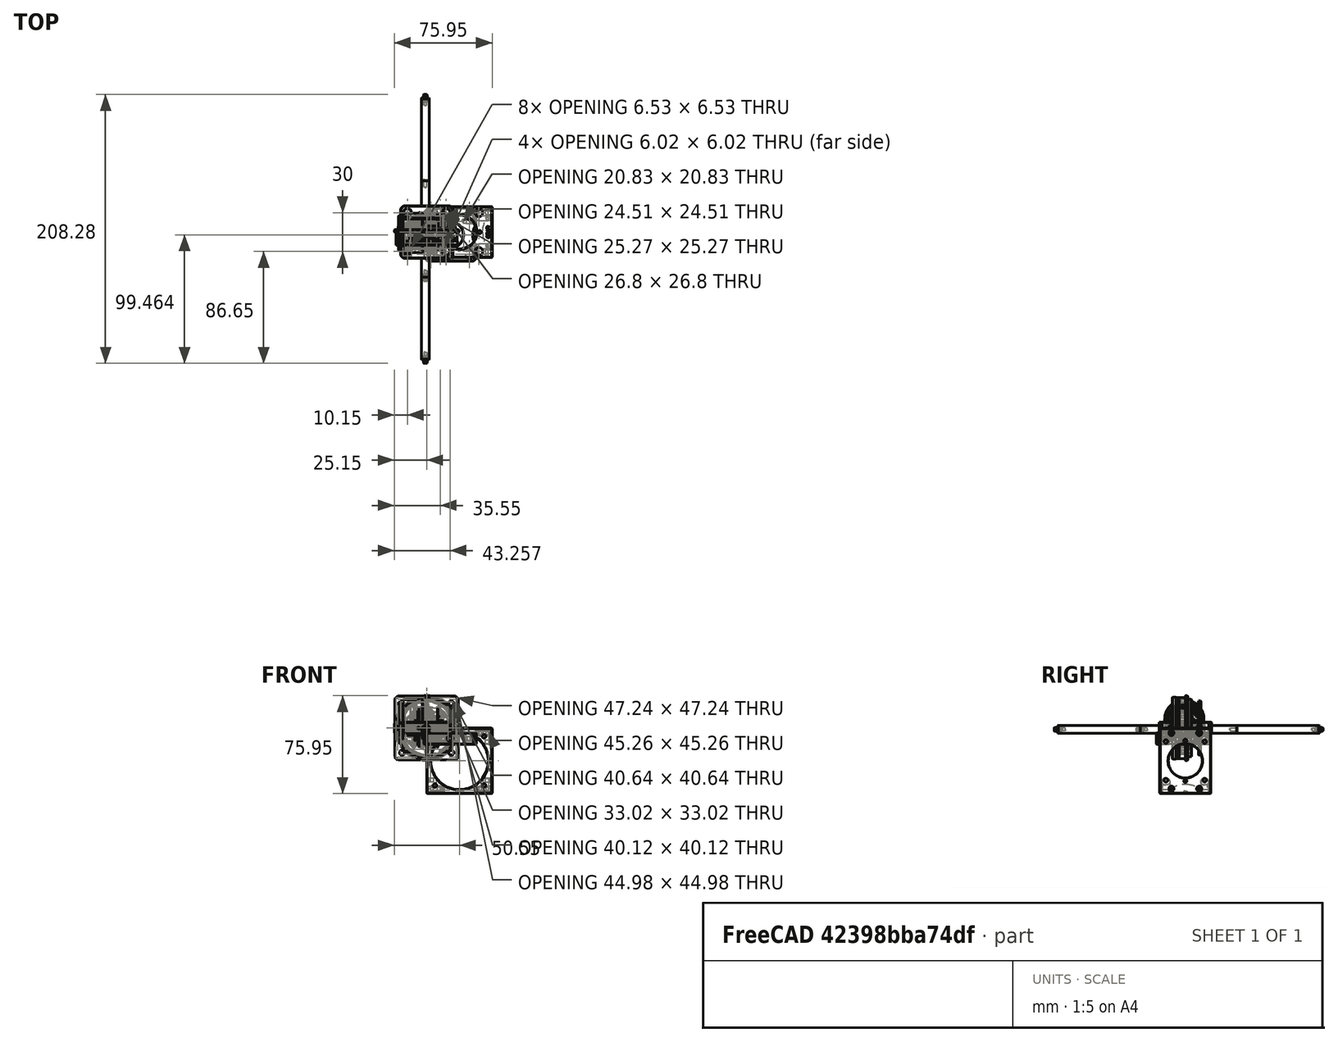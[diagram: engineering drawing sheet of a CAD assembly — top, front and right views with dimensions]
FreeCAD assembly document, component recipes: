
FREECAD ASSEMBLY — COMPONENT RECIPES ("optical-system")

This assembly document has 22 components, labeled P0..P21 below (a component is one placed body or linked part). 1 of them carries a construction recipe — the FreeCAD feature program that regenerates the part from scratch, quoted from this document or its linked companion documents; the rest are supplied as boundary geometry only. No exploded tour is included for this assembly.
COMPONENT P0 — geometry summary ("AC254-040-A-ML001"; no construction recipe available for this part):
  bounding box: 30.5 x 30.5 x 18.5 mm
  tessellated surface: 17,778 triangles
  volume: 9000 mm^3 (52% of its bounding box)
  symmetry: revolution-symmetric about the z axis through its bounding-box center; mirror-symmetric across its x mid-plane, y mid-plane
COMPONENT P1 — geometry summary ("AC254-040-A-ML002"; no construction recipe available for this part):
  bounding box: 30.5 x 30.5 x 18.5 mm
  tessellated surface: 17,778 triangles
  volume: 9000 mm^3 (52% of its bounding box)
  symmetry: revolution-symmetric about the z axis through its bounding-box center; mirror-symmetric across its x mid-plane, y mid-plane
COMPONENT P2 — geometry summary ("AC254-060-A-ML-001"; no construction recipe available for this part):
  bounding box: 30.5 x 30.5 x 17.8 mm
  tessellated surface: 17,160 triangles
  volume: 8517 mm^3 (51% of its bounding box)
  symmetry: revolution-symmetric about the y axis through its bounding-box center; mirror-symmetric across its x mid-plane, z mid-plane
COMPONENT P3 — geometry summary ("B3CR-001"; no construction recipe available for this part):
  bounding box: 50.3 x 50.3 x 14.7 mm
  tessellated surface: 65,470 triangles
  volume: 24011 mm^3 (64% of its bounding box)
COMPONENT P4 — recipe-attached ("BST10R002", modeled in this document).
Construction recipe (the document's own serialized feature program — sketch geometry with constraints, then the solid features built on it; lengths are millimeters unless a unit is written):

FEATURE [PartDesign::FeatureBase] BaseFeature
  BaseFeature = -> Part__Feature051
  Suppressed = false
FEATURE [Sketcher::SketchObject] Sketch
  ArcFitTolerance = 1e-06
  AttachmentSupport = -> [BaseFeature]
  FullyConstrained = true
  MakeInternals = false
  MapMode = 5
  Placement = pos=(0,-12.5,0) rot=(1,0,0;1.5708rad)
  sketch-geometry (5):
    g0: LineSegment StartX=-18 StartY=-0.75 StartZ=0 EndX=18 EndY=-0.75 EndZ=0
    g1: LineSegment StartX=18 StartY=-0.75 StartZ=0 EndX=18 EndY=0.75 EndZ=0
    g2: LineSegment StartX=18 StartY=0.75 StartZ=0 EndX=-18 EndY=0.75 EndZ=0
    g3: LineSegment StartX=-18 StartY=0.75 StartZ=0 EndX=-18 EndY=-0.75 EndZ=0
    g4: GeomPoint [constr] X=0 Y=0 Z=0
  constraints (12):
    c: Coincident(g0,g1)
    c: Coincident(g1,g2)
    c: Coincident(g2,g3)
    c: Coincident(g3,g0)
    c: Horizontal(g0)
    c: Horizontal(g2)
    c: Vertical(g1)
    c: Vertical(g3)
    c: Symmetric(g2,g0,g4)
    c: Distance(g1,g3) = 36
    c: Distance(g0,g2) = 1.5
    c: Coincident(g4,g-1)
FEATURE [PartDesign::Pocket] Pocket
  BaseFeature = -> BaseFeature
  Direction = (0,1,-2e-16)
  Length = 8
  Length2 = 5
  Profile = -> Sketch
  ReferenceAxis = -> Sketch [N_Axis]
  Refine = true
  Suppressed = false
  Type = 0
FEATURE [PartDesign::Body] Body
  AllowCompound = false
  BaseFeature = -> Part__Feature051
  Group = -> [BaseFeature,Sketch,Pocket]
  Origin = -> Origin014
  Tip = -> Pocket
COMPONENT P5 — geometry summary ("C6WA-001"; no construction recipe available for this part):
  bounding box: 49.8 x 49.8 x 12.1 mm
  tessellated surface: 19,482 triangles
  volume: 6420 mm^3 (21% of its bounding box)
  symmetry: 4-fold rotationally symmetric about the x axis; mirror-symmetric across its y mid-plane, z mid-plane
COMPONENT P6 — geometry summary ("C6WR001"; no construction recipe available for this part):
  bounding box: 50.8 x 50.8 x 39.6 mm
  tessellated surface: 57,528 triangles
  volume: 28065 mm^3 (27% of its bounding box)
  symmetry: 2-fold rotationally symmetric about the x axis; 2-fold rotationally symmetric about the z axis; mirror-symmetric across its x mid-plane, y mid-plane, z mid-plane
COMPONENT P7 — geometry summary ("CP33-001"; no construction recipe available for this part):
  bounding box: 40.6 x 40.6 x 8.9 mm
  tessellated surface: 31,646 triangles
  volume: 8352 mm^3 (57% of its bounding box)
  symmetry: 2-fold rotationally symmetric about the x axis; mirror-symmetric across its z mid-plane
COMPONENT P8 — geometry summary ("CP33-002"; no construction recipe available for this part):
  bounding box: 40.6 x 40.6 x 8.9 mm
  tessellated surface: 31,646 triangles
  volume: 8352 mm^3 (57% of its bounding box)
  symmetry: 2-fold rotationally symmetric about the x axis; mirror-symmetric across its z mid-plane
COMPONENT P9 — geometry summary ("CP33-003"; no construction recipe available for this part):
  bounding box: 40.6 x 40.6 x 8.9 mm
  tessellated surface: 31,646 triangles
  volume: 8352 mm^3 (57% of its bounding box)
  symmetry: 2-fold rotationally symmetric about the x axis; mirror-symmetric across its z mid-plane
COMPONENT P10 — geometry summary ("CP33-004"; no construction recipe available for this part):
  bounding box: 40.6 x 40.6 x 8.9 mm
  tessellated surface: 31,646 triangles
  volume: 8352 mm^3 (57% of its bounding box)
  symmetry: 2-fold rotationally symmetric about the x axis; mirror-symmetric across its z mid-plane
COMPONENT P11 — geometry summary ("CP42-001"; no construction recipe available for this part):
  bounding box: 40.6 x 40.6 x 8.9 mm
  tessellated surface: 33,740 triangles
  volume: 9819 mm^3 (67% of its bounding box)
  symmetry: 2-fold rotationally symmetric about the y axis; mirror-symmetric across its x mid-plane, z mid-plane
COMPONENT P12 — geometry summary ("ER3-001"; no construction recipe available for this part):
  bounding box: 78.7 x 6.0 x 6.0 mm
  tessellated surface: 11,270 triangles
  volume: 2126 mm^3 (75% of its bounding box)
  symmetry: revolution-symmetric about the z axis through its bounding-box center; mirror-symmetric across its x mid-plane, y mid-plane
COMPONENT P13 — geometry summary ("ER3-002"; no construction recipe available for this part):
  bounding box: 78.7 x 6.0 x 6.0 mm
  tessellated surface: 11,270 triangles
  volume: 2126 mm^3 (75% of its bounding box)
  symmetry: revolution-symmetric about the z axis through its bounding-box center; mirror-symmetric across its x mid-plane, y mid-plane
COMPONENT P14 — geometry summary ("ER3-003"; no construction recipe available for this part):
  bounding box: 78.7 x 6.0 x 6.0 mm
  tessellated surface: 11,270 triangles
  volume: 2126 mm^3 (75% of its bounding box)
  symmetry: revolution-symmetric about the z axis through its bounding-box center; mirror-symmetric across its x mid-plane, y mid-plane
COMPONENT P15 — geometry summary ("ER3-004"; no construction recipe available for this part):
  bounding box: 78.7 x 6.0 x 6.0 mm
  tessellated surface: 11,270 triangles
  volume: 2126 mm^3 (75% of its bounding box)
  symmetry: revolution-symmetric about the z axis through its bounding-box center; mirror-symmetric across its x mid-plane, y mid-plane
COMPONENT P16 — geometry summary ("ER8-001"; no construction recipe available for this part):
  bounding box: 208.3 x 6.0 x 6.0 mm
  tessellated surface: 18,188 triangles
  volume: 5735 mm^3 (77% of its bounding box)
  symmetry: 2-fold rotationally symmetric about the x axis; revolution-symmetric about the y axis through its bounding-box center; 2-fold rotationally symmetric about the z axis; mirror-symmetric across its x mid-plane, y mid-plane, z mid-plane
COMPONENT P17 — geometry summary ("ER8-002"; no construction recipe available for this part):
  bounding box: 208.3 x 6.0 x 6.0 mm
  tessellated surface: 18,188 triangles
  volume: 5735 mm^3 (77% of its bounding box)
  symmetry: 2-fold rotationally symmetric about the x axis; revolution-symmetric about the y axis through its bounding-box center; 2-fold rotationally symmetric about the z axis; mirror-symmetric across its x mid-plane, y mid-plane, z mid-plane
COMPONENT P18 — geometry summary ("ER8-003"; no construction recipe available for this part):
  bounding box: 208.3 x 6.0 x 6.0 mm
  tessellated surface: 18,188 triangles
  volume: 5735 mm^3 (77% of its bounding box)
  symmetry: 2-fold rotationally symmetric about the x axis; revolution-symmetric about the y axis through its bounding-box center; 2-fold rotationally symmetric about the z axis; mirror-symmetric across its x mid-plane, y mid-plane, z mid-plane
COMPONENT P19 — geometry summary ("ER8-004"; no construction recipe available for this part):
  bounding box: 208.3 x 6.0 x 6.0 mm
  tessellated surface: 18,188 triangles
  volume: 5735 mm^3 (77% of its bounding box)
  symmetry: 2-fold rotationally symmetric about the x axis; revolution-symmetric about the y axis through its bounding-box center; 2-fold rotationally symmetric about the z axis; mirror-symmetric across its x mid-plane, y mid-plane, z mid-plane
COMPONENT P20 — geometry summary ("FFM-1-001"; no construction recipe available for this part):
  bounding box: 32.3 x 32.3 x 7.4 mm
  tessellated surface: 52,722 triangles
  volume: 2229 mm^3 (29% of its bounding box)
COMPONENT P21 — geometry summary ("NE07A-001"; no construction recipe available for this part):
  bounding box: 30.5 x 30.5 x 11.4 mm
  tessellated surface: 10,714 triangles
  volume: 2733 mm^3 (26% of its bounding box)
  symmetry: revolution-symmetric about the y axis through its bounding-box center; mirror-symmetric across its x mid-plane, z mid-plane
PROVENANCE & LICENSES
A FreeCAD (.FCStd) document from a public repository crawl; recipes are the document's own serialized feature recipes (and, for linked parts, companion documents' recipes).
License: other.
